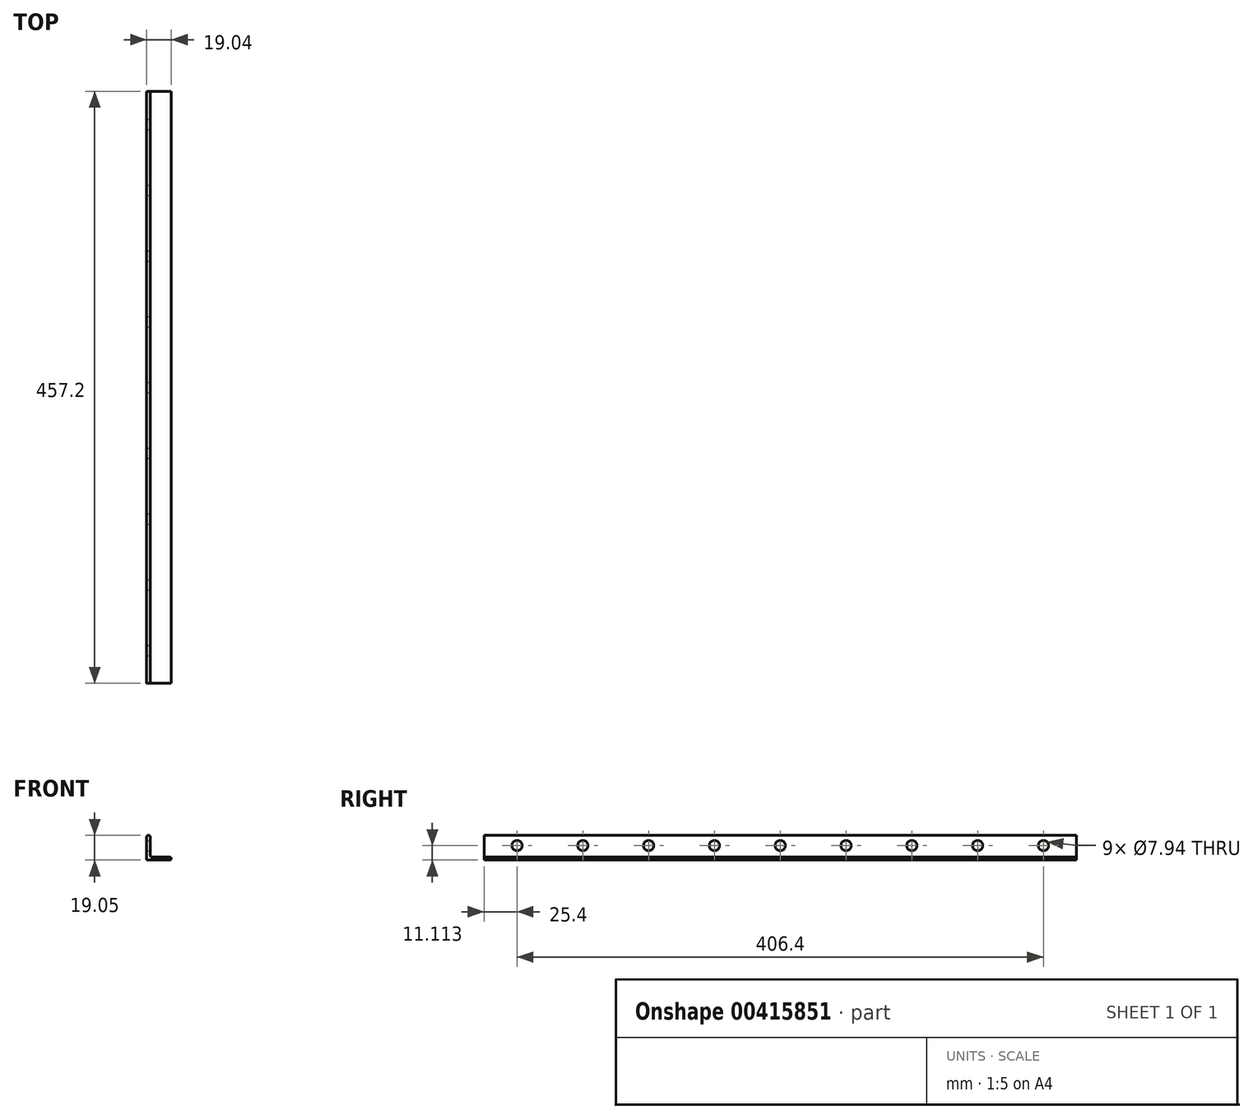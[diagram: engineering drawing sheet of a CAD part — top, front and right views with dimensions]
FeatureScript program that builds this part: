
annotation { "Feature Type Name" : "Feature", "Feature Type Description" : "" }
export const myFeature = defineFeature(function(context is Context, id is Id, definition is map)
    precondition{}
    {
        {
            var Q0;
            Q0=qCreatedBy(makeId("Front.planeOp"),FACE);
            var sketch = newSketch(context, id + "F0", { "sketchPlane" : qUnion([Q0])});
            skLineSegment(sketch, "E0.bottom", {"start": v(0, 0) * mm, "end": v(2.73, 0) * mm});
            skLineSegment(sketch, "E0.top", {"start": v(0, 19.05) * mm, "end": v(2.73, 19.05) * mm});
            skLineSegment(sketch, "E0.left", {"start": v(0, 0) * mm, "end": v(0, 19.05) * mm});
            skLineSegment(sketch, "E0.right", {"start": v(2.73, 2.26) * mm, "end": v(2.73, 19.05) * mm});
            skLineSegment(sketch, "E1.bottom", {"start": v(0, 0) * mm, "end": v(19.05, 0) * mm});
            skLineSegment(sketch, "E1.top", {"start": v(2.73, 2.26) * mm, "end": v(19.05, 2.26) * mm});
            skLineSegment(sketch, "E1.left", {"start": v(0, 0) * mm, "end": v(0, 2.26) * mm});
            skLineSegment(sketch, "E1.right", {"start": v(19.05, 0) * mm, "end": v(19.05, 2.26) * mm});
            skSolve(sketch);
        }
        {
            var Q0;
            Q0=makeQuery(id+"F0.imprint","IMPRINT",FACE,{"disambiguationData":[TD([[makeQuery(id+"F0.imprint","IMPRINT",EDGE,{"derivedFrom":sQuery(id+"F0.wireOp",EDGE,"E0.top")}),-1.0]])]});
            extrude(context, id + "F1", {"entities" : qUnion([Q0]), "endBound" : BoundingType.SYMMETRIC, "depth" : 457.2 * mm});
        }
        {
            var Q0;
            Q0=makeQuery(id+"F1.opExtrude","SWEPT_FACE",FACE,{"disambiguationData":[OSD([sQuery(id+"F0.wireOp",EDGE,"E0.right")])]});
            var sketch = newSketch(context, id + "F2", { "sketchPlane" : qUnion([Q0])});
            skCircle(sketch, "E2", {"center": v(-203.2, 11.11) * mm, "radius": 3.97 * mm});
            skCircle(sketch, "E3.1.0.0", {"center": v(-152.4, 11.11) * mm, "radius": 3.97 * mm});
            skCircle(sketch, "E3.2.0.0", {"center": v(-101.6, 11.11) * mm, "radius": 3.97 * mm});
            skCircle(sketch, "E3.3.0.0", {"center": v(-50.8, 11.11) * mm, "radius": 3.97 * mm});
            skCircle(sketch, "E3.4.0.0", {"center": v(0, 11.11) * mm, "radius": 3.97 * mm});
            skCircle(sketch, "E3.5.0.0", {"center": v(50.8, 11.11) * mm, "radius": 3.97 * mm});
            skCircle(sketch, "E3.6.0.0", {"center": v(101.6, 11.11) * mm, "radius": 3.97 * mm});
            skCircle(sketch, "E3.7.0.0", {"center": v(152.4, 11.11) * mm, "radius": 3.97 * mm});
            skCircle(sketch, "E3.8.0.0", {"center": v(203.2, 11.11) * mm, "radius": 3.97 * mm});
            skLineSegment(sketch, "E3.direction1", {"start": v(-203.2, 11.11) * mm, "end": v(-152.4, 11.11) * mm, "construction": true});
            skSolve(sketch);
        }
        {
            var Q0;
            Q0=sQuery(id+"F2.wireOp",VERTEX,"E3.direction1.start");
            var Q1;
            Q1=sQuery(id+"F2.wireOp",VERTEX,"E3.1.0.0.center");
            var Q2;
            Q2=sQuery(id+"F2.wireOp",VERTEX,"E3.2.0.0.center");
            var Q3;
            Q3=sQuery(id+"F2.wireOp",VERTEX,"E3.3.0.0.center");
            var Q4;
            Q4=sQuery(id+"F2.wireOp",VERTEX,"E3.6.0.0.center");
            var Q5;
            Q5=sQuery(id+"F2.wireOp",VERTEX,"E3.5.0.0.center");
            var Q6;
            Q6=sQuery(id+"F2.wireOp",VERTEX,"E3.4.0.0.center");
            var Q7;
            Q7=sQuery(id+"F2.wireOp",VERTEX,"E3.7.0.0.center");
            var Q8;
            Q8=sQuery(id+"F2.wireOp",VERTEX,"E3.8.0.0.center");
            var Q9;
            Q9=makeQuery(id+"F1.opExtrude","SWEPT_BODY",BODY,{"disambiguationData":[OSD([sQuery(id+"F0.wireOp",EDGE,"E0.top"),sQuery(id+"F0.wireOp",EDGE,"E0.left"),sQuery(id+"F0.wireOp",EDGE,"E0.right"),sQuery(id+"F0.wireOp",EDGE,"E1.bottom"),sQuery(id+"F0.wireOp",EDGE,"E1.top"),sQuery(id+"F0.wireOp",EDGE,"E1.left"),sQuery(id+"F0.wireOp",EDGE,"E1.right")])]});
            hole(context, id + "F3", {"style" : HoleStyle.SIMPLE, "endStyle" : HoleEndStyle.THROUGH, "holeDiameter" : 7.94 * mm, "isTappedThrough" : true, "tappedDepth" : 12.7 * mm, "tapClearance" : 3, "locations" : qUnion([Q0, Q1, Q2, Q3, Q4, Q5, Q6, Q7, Q8]), "scope" : qUnion([Q9])});
        }
        {
            var Q0;
            Q0=makeQuery(id+"F1.opExtrude","SWEPT_EDGE",EDGE,{"disambiguationData":[OSD([sQuery(id+"F0.wireOp",EDGE,"E0.right"),sQuery(id+"F0.wireOp",EDGE,"E1.top")])]});
            var Q1;
            Q1=makeQuery(id+"F1.opExtrude","SWEPT_EDGE",EDGE,{"disambiguationData":[OSD([sQuery(id+"F0.wireOp",EDGE,"E0.top"),sQuery(id+"F0.wireOp",EDGE,"E0.left")])]});
            var Q2;
            Q2=makeQuery(id+"F1.opExtrude","SWEPT_EDGE",EDGE,{"disambiguationData":[OSD([sQuery(id+"F0.wireOp",EDGE,"E0.top"),sQuery(id+"F0.wireOp",EDGE,"E0.right")])]});
            var Q3;
            Q3=makeQuery(id+"F1.opExtrude","SWEPT_EDGE",EDGE,{"disambiguationData":[OSD([sQuery(id+"F0.wireOp",EDGE,"E1.top"),sQuery(id+"F0.wireOp",EDGE,"E1.right")])]});
            var Q4;
            Q4=makeQuery(id+"F1.opExtrude","SWEPT_EDGE",EDGE,{"disambiguationData":[OSD([sQuery(id+"F0.wireOp",EDGE,"E1.bottom"),sQuery(id+"F0.wireOp",EDGE,"E1.right")])]});
            var Q5;
            Q5=makeQuery(id+"F1.opExtrude","SWEPT_EDGE",EDGE,{"disambiguationData":[OSD([sQuery(id+"F0.wireOp",EDGE,"E1.bottom"),sQuery(id+"F0.wireOp",EDGE,"E1.left")])]});
            fillet(context, id + "F4", {"entities" : qUnion([Q0, Q1, Q2, Q3, Q4, Q5]), "radius" : 1.27 * mm, "tangentPropagation" : true, "allowEdgeOverflow" : false});
        }
    });
